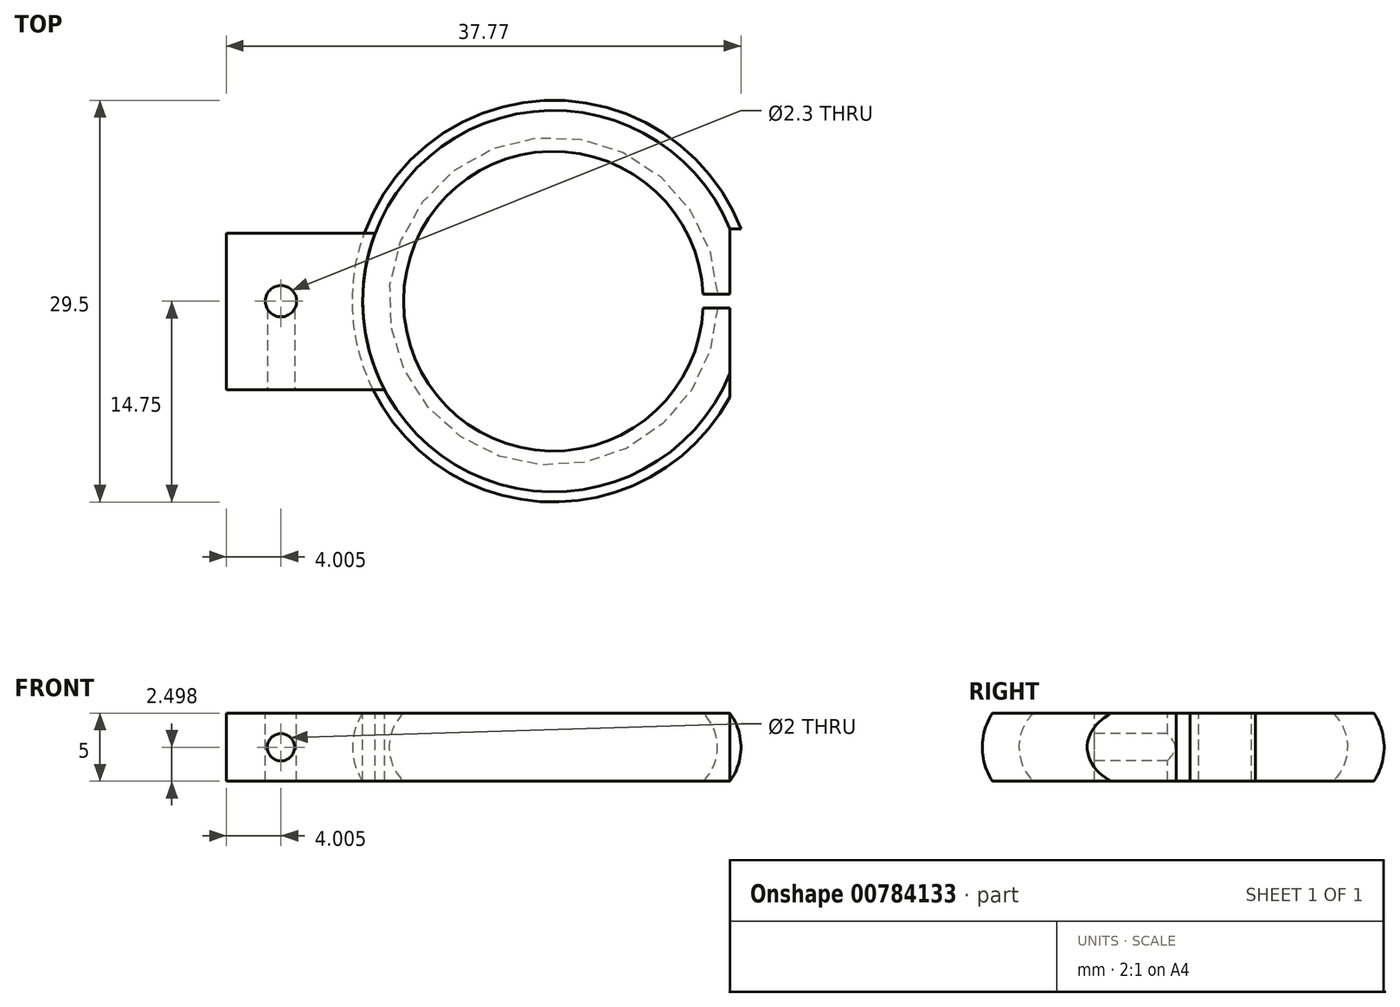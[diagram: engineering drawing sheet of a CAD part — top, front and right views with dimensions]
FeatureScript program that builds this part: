
annotation { "Feature Type Name" : "Feature", "Feature Type Description" : "" }
export const myFeature = defineFeature(function(context is Context, id is Id, definition is map)
    precondition{}
    {
        {
            var Q0;
            Q0=qCreatedBy(makeId("Front.planeOp"),FACE);
            var sketch = newSketch(context, id + "F0", { "sketchPlane" : qUnion([Q0])});
            skLineSegment(sketch, "E0", {"start": v(6.35, 6.82) * mm, "end": v(6.35, -1.39) * mm});
            skCircle(sketch, "E1", {"center": v(-4.65, 3.56) * mm, "radius": 2.5 * mm});
            skArc(sketch, "E2", {"start": v(-4.65, 6.06) * mm, "mid": v(-5.7, 3.56) * mm, "end": v(-4.65, 1.06) * mm});
            skLineSegment(sketch, "E3", {"start": v(-4.65, 6.06) * mm, "end": v(-7.65, 6.06) * mm});
            skLineSegment(sketch, "E4", {"start": v(-7.65, 6.06) * mm, "end": v(-7.65, 1.06) * mm});
            skLineSegment(sketch, "E5", {"start": v(-7.65, 1.06) * mm, "end": v(-4.65, 1.06) * mm});
            skArc(sketch, "E6", {"start": v(-7.65, 6.06) * mm, "mid": v(-8.4, 3.56) * mm, "end": v(-7.65, 1.06) * mm});
            skSolve(sketch);
        }
        {
            var Q0;
            {var subQ0=sQuery(id+"F0.wireOp",EDGE,"E2");Q0=makeQuery(id+"F0.imprint","IMPRINT",FACE,{"disambiguationData":[TD([[makeQuery(id+"F0.imprint","IMPRINT",EDGE,{"derivedFrom":subQ0}),-1.0]])]});}
            var Q1;
            {var subQ0=sQuery(id+"F0.wireOp",EDGE,"E3");Q1=makeQuery(id+"F0.imprint","IMPRINT",FACE,{"disambiguationData":[TD([[makeQuery(id+"F0.imprint","IMPRINT",EDGE,{"derivedFrom":subQ0}),1.0]])]});}
            var Q2;
            Q2=makeQuery(id+"F0.imprint","IMPRINT",FACE,{"disambiguationData":[TD([[makeQuery(id+"F0.imprint","IMPRINT",EDGE,{"derivedFrom":sQuery(id+"F0.wireOp",EDGE,"E4")}),-1.0]])]});
            var Q3;
            Q3=sQuery(id+"F0.wireOp",EDGE,"E0");
            revolve(context, id + "F1", {"surfaceOperationType" : NewSurfaceOperationType.NEW, "entities" : qUnion([Q0, Q1, Q2]), "axis" : qUnion([Q3]), "revolveType" : RevolveType.FULL});
        }
        {
            var Q0;
            Q0=makeQuery(id+"F1.opRevolve","SWEPT_FACE",FACE,{"disambiguationData":[OSD([sQuery(id+"F0.wireOp",EDGE,"E3")])]});
            var sketch = newSketch(context, id + "F2", { "sketchPlane" : qUnion([Q0])});
            skLineSegment(sketch, "E7.bottom", {"start": v(18.93, -0.5) * mm, "end": v(24.93, -0.5) * mm});
            skLineSegment(sketch, "E7.top", {"start": v(18.93, -5.3) * mm, "end": v(24.93, -5.3) * mm});
            skLineSegment(sketch, "E7.left", {"start": v(18.93, -0.5) * mm, "end": v(18.93, -5.3) * mm});
            skLineSegment(sketch, "E7.right", {"start": v(24.93, -0.5) * mm, "end": v(24.93, -5.3) * mm});
            skLineSegment(sketch, "E8.bottom", {"start": v(18.93, 0.5) * mm, "end": v(24.93, 0.5) * mm});
            skLineSegment(sketch, "E8.top", {"start": v(18.93, 5.3) * mm, "end": v(24.93, 5.3) * mm});
            skLineSegment(sketch, "E8.left", {"start": v(18.93, 0.5) * mm, "end": v(18.93, 5.3) * mm});
            skLineSegment(sketch, "E8.right", {"start": v(24.93, 0.5) * mm, "end": v(24.93, 5.3) * mm});
            skLineSegment(sketch, "E9.bottom", {"start": v(-5.32, -6.5) * mm, "end": v(-17.65, -6.5) * mm});
            skLineSegment(sketch, "E9.top", {"start": v(-5.32, 5) * mm, "end": v(-17.65, 5) * mm});
            skLineSegment(sketch, "E9.left", {"start": v(-5.32, -6.5) * mm, "end": v(-5.32, 5) * mm});
            skLineSegment(sketch, "E9.right", {"start": v(-17.65, -6.5) * mm, "end": v(-17.65, 5) * mm});
            skCircle(sketch, "E10", {"center": v(-13.65, 0) * mm, "radius": 1.15 * mm});
            skPoint(sketch, "E11", {"position": v(6.35, 0) * mm});
            skSolve(sketch);
        }
        {
            var Q0;
            {var subQ0=sQuery(id+"F2.wireOp",EDGE,"E9.right");Q0=makeQuery(id+"F2.imprint","IMPRINT",FACE,{"disambiguationData":[TD([[makeQuery(id+"F2.imprint","IMPRINT",EDGE,{"derivedFrom":subQ0}),-1.0]])]});}
            var Q1;
            {var subQ0=sQuery(id+"F2.wireOp",EDGE,"E7.right");Q1=makeQuery(id+"F2.imprint","IMPRINT",FACE,{"disambiguationData":[TD([[makeQuery(id+"F2.imprint","IMPRINT",EDGE,{"derivedFrom":subQ0}),-1.0]])]});}
            var Q2;
            {var subQ0=sQuery(id+"F2.wireOp",EDGE,"E8.right");Q2=makeQuery(id+"F2.imprint","IMPRINT",FACE,{"disambiguationData":[TD([[makeQuery(id+"F2.imprint","IMPRINT",EDGE,{"derivedFrom":subQ0}),1.0]])]});}
            extrude(context, id + "F3", {"entities" : qUnion([Q0, Q1, Q2]), "oppositeDirection" : true, "depth" : 5 * mm, "offsetDistance" : 25 * mm});
        }
        {
            var Q0;
            Q0=makeQuery(id+"F3.opExtrude","SWEPT_FACE",FACE,{"disambiguationData":[OSD([sQuery(id+"F2.wireOp",EDGE,"E9.bottom")])]});
            var sketch = newSketch(context, id + "F4", { "sketchPlane" : qUnion([Q0])});
            skCircle(sketch, "E12", {"center": v(-13.65, 3.56) * mm, "radius": 1 * mm});
            skPoint(sketch, "E12.centerSnap0", {"position": v(-17.65, 3.56) * mm});
            skSolve(sketch);
        }
        {
            var Q0;
            Q0=makeQuery(id+"F4.imprint","IMPRINT",FACE,{"disambiguationData":[TD([[makeQuery(id+"F4.imprint","IMPRINT",EDGE,{"derivedFrom":sQuery(id+"F4.wireOp",EDGE,"E12")}),1.0]])]});
            extrude(context, id + "F5", {"entities" : qUnion([Q0]), "operationType" : NewBodyOperationType.REMOVE, "oppositeDirection" : true, "depth" : 6 * mm, "offsetDistance" : 25 * mm});
        }
        {
            var Q0;
            Q0=makeQuery(id+"F3.opExtrude","SWEPT_FACE",FACE,{"disambiguationData":[OSD([sQuery(id+"F2.wireOp",EDGE,"E7.top")])]});
            var sketch = newSketch(context, id + "F6", { "sketchPlane" : qUnion([Q0])});
            skCircle(sketch, "E13", {"center": v(22.33, 3.56) * mm, "radius": 1 * mm});
            skPoint(sketch, "E13.centerSnap0", {"position": v(24.93, 3.56) * mm});
            skSolve(sketch);
        }
        {
            var Q0;
            Q0=makeQuery(id+"F6.imprint","IMPRINT",FACE,{"disambiguationData":[TD([[makeQuery(id+"F6.imprint","IMPRINT",EDGE,{"derivedFrom":sQuery(id+"F6.wireOp",EDGE,"E13")}),1.0]])]});
            extrude(context, id + "F7", {"entities" : qUnion([Q0]), "operationType" : NewBodyOperationType.REMOVE, "oppositeDirection" : true, "depth" : 25 * mm, "offsetDistance" : 25 * mm});
        }
        {
            var Q0;
            Q0=makeQuery(id+"F3.opExtrude","SWEPT_FACE",FACE,{"disambiguationData":[OSD([sQuery(id+"F2.wireOp",EDGE,"E8.top")])]});
            var sketch = newSketch(context, id + "F8", { "sketchPlane" : qUnion([Q0])});
            skCircle(sketch, "E14", {"center": v(-22.33, 3.56) * mm, "radius": 1 * mm});
            skPoint(sketch, "E14.centerSnap0", {"position": v(-24.93, 3.56) * mm});
            skSolve(sketch);
        }
        {
            var Q0;
            Q0=makeQuery(id+"F8.imprint","IMPRINT",FACE,{"disambiguationData":[TD([[makeQuery(id+"F8.imprint","IMPRINT",EDGE,{"derivedFrom":sQuery(id+"F8.wireOp",EDGE,"E14")}),1.0]])]});
            extrude(context, id + "F9", {"entities" : qUnion([Q0]), "operationType" : NewBodyOperationType.REMOVE, "oppositeDirection" : true, "depth" : 25 * mm, "offsetDistance" : 25 * mm});
        }
        {
            var Q0;
            Q0=makeQuery(id+"F1.opRevolve","SWEPT_FACE",FACE,{"disambiguationData":[OSD([sQuery(id+"F0.wireOp",EDGE,"E3")])]});
            var sketch = newSketch(context, id + "F10", { "sketchPlane" : qUnion([Q0])});
            skLineSegment(sketch, "E15.bottom", {"start": v(21.95, 0.5) * mm, "end": v(16.1, 0.5) * mm});
            skLineSegment(sketch, "E15.top", {"start": v(21.95, -0.5) * mm, "end": v(16.1, -0.5) * mm});
            skLineSegment(sketch, "E15.left", {"start": v(21.95, 0.5) * mm, "end": v(21.95, -0.5) * mm});
            skLineSegment(sketch, "E15.right", {"start": v(16.1, 0.5) * mm, "end": v(16.1, -0.5) * mm});
            skSolve(sketch);
        }
        {
            var Q0;
            {var subQ0=sQuery(id+"F10.wireOp",EDGE,"E15.bottom");var subQ1=sQuery(id+"F0.wireOp",EDGE,"E3");var subQ2=makeQuery(id+"F1.opRevolve","SWEPT_EDGE",EDGE,{"disambiguationData":[OSD([subQ1,sQuery(id+"F0.wireOp",EDGE,"E4"),sQuery(id+"F0.wireOp",EDGE,"E6")])]});var subQ3=makeQuery(id+"F10.imprint","INTERSECT",VERTEX,{"derivedFrom":[subQ2,subQ0]});Q0=makeQuery(id+"F10.imprint","IMPRINT",FACE,{"disambiguationData":[TD([[makeQuery(id+"F10.imprint","IMPRINT",EDGE,{"disambiguationData":[TD([[subQ3,-1.0]])],"derivedFrom":subQ0}),1.0]])]});}
            var Q1;
            {var subQ0=sQuery(id+"F10.wireOp",EDGE,"E15.left");Q1=makeQuery(id+"F10.imprint","IMPRINT",FACE,{"disambiguationData":[TD([[makeQuery(id+"F10.imprint","IMPRINT",EDGE,{"derivedFrom":subQ0}),-1.0]])]});}
            extrude(context, id + "F11", {"entities" : qUnion([Q0, Q1]), "operationType" : NewBodyOperationType.REMOVE, "oppositeDirection" : true, "depth" : 25 * mm, "offsetDistance" : 25 * mm});
        }
    });
